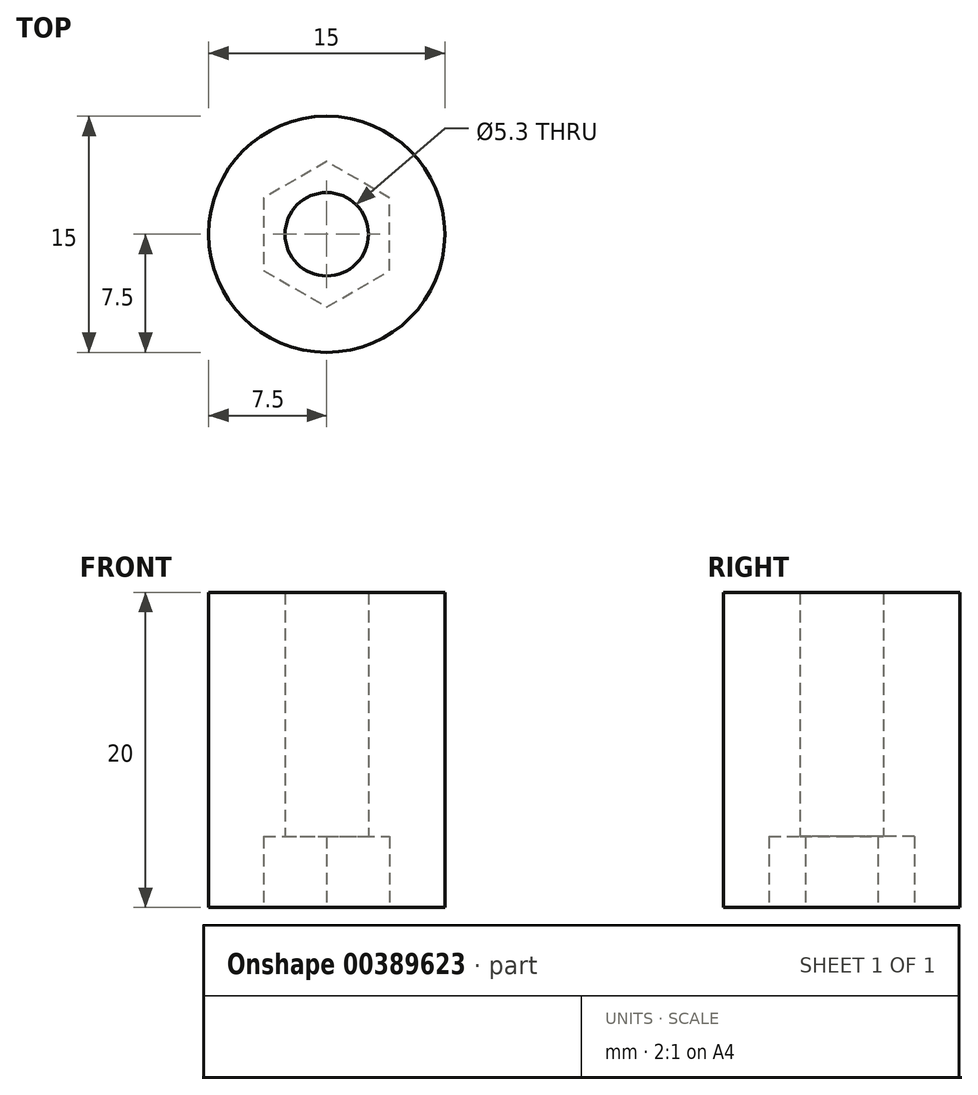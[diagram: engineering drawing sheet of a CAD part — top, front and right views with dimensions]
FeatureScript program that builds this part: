
annotation { "Feature Type Name" : "Feature", "Feature Type Description" : "" }
export const myFeature = defineFeature(function(context is Context, id is Id, definition is map)
    precondition{}
    {
        {
            var Q0;
            Q0=qCreatedBy(makeId("Top.planeOp"),FACE);
            var sketch = newSketch(context, id + "F0", { "sketchPlane" : qUnion([Q0])});
            skCircle(sketch, "E0", {"center": v(0, 0) * mm, "radius": 2.65 * mm});
            skCircle(sketch, "E1", {"center": v(0, 0) * mm, "radius": 7.5 * mm});
            skSolve(sketch);
        }
        {
            var Q0;
            Q0 = qSketchRegion(id + "F0", true);
            extrude(context, id + "F1", {"entities" : qUnion([Q0]), "depth" : 20 * mm});
        }
        {
            var Q0;
            Q0=makeQuery(id+"F1.opExtrude","CAP_FACE",FACE,{"disambiguationData":[OSD([sQuery(id+"F0.wireOp",EDGE,"E0"),sQuery(id+"F0.wireOp",EDGE,"E1")])],"isStart":true});
            var sketch = newSketch(context, id + "F2", { "sketchPlane" : qUnion([Q0])});
            skCircle(sketch, "E2.cCircle", {"center": v(0, 0) * mm, "radius": 4 * mm, "construction": true});
            skLineSegment(sketch, "E2.0", {"start": v(0, 4.62) * mm, "end": v(4, 2.3) * mm});
            skLineSegment(sketch, "E2.1", {"start": v(4, 2.3) * mm, "end": v(4, -2.3) * mm});
            skLineSegment(sketch, "E2.2", {"start": v(4, -2.3) * mm, "end": v(0, -4.62) * mm});
            skLineSegment(sketch, "E2.3", {"start": v(0, -4.62) * mm, "end": v(-4, -2.3) * mm});
            skLineSegment(sketch, "E2.4", {"start": v(-4, -2.3) * mm, "end": v(-4, 2.3) * mm});
            skLineSegment(sketch, "E2.5", {"start": v(-4, 2.3) * mm, "end": v(0, 4.62) * mm});
            skPoint(sketch, "E2.0.midPoint", {"position": v(2, 3.46) * mm});
            skSolve(sketch);
        }
        {
            var Q0;
            Q0 = qSketchRegion(id + "F2", true);
            extrude(context, id + "F3", {"entities" : qUnion([Q0]), "operationType" : NewBodyOperationType.REMOVE, "oppositeDirection" : true, "depth" : 4.5 * mm});
        }
    });
